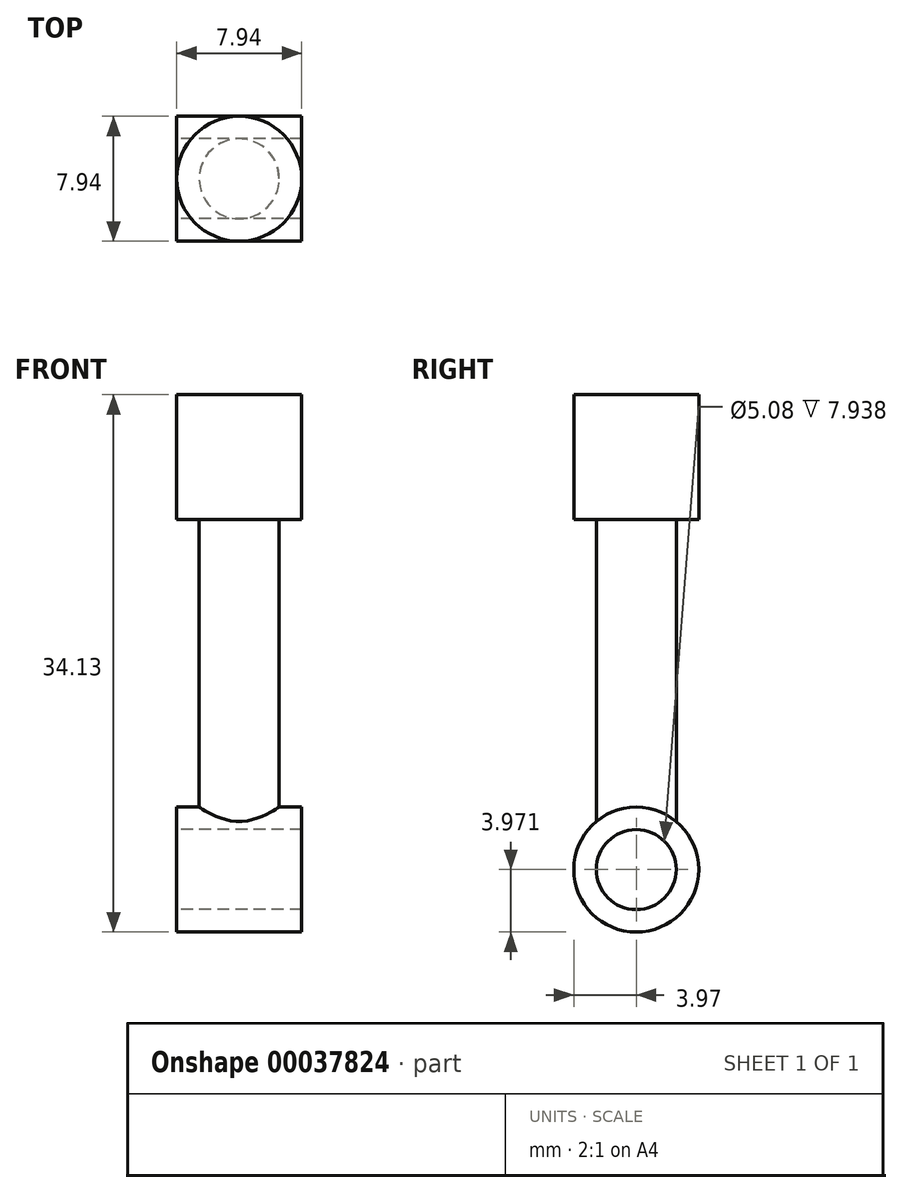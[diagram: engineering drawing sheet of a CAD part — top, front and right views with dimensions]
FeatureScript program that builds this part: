
annotation { "Feature Type Name" : "Feature", "Feature Type Description" : "" }
export const myFeature = defineFeature(function(context is Context, id is Id, definition is map)
    precondition{}
    {
        {
            var Q0;
            Q0=qCreatedBy(makeId("Top.planeOp"),FACE);
            var sketch = newSketch(context, id + "F0", { "sketchPlane" : qUnion([Q0])});
            skCircle(sketch, "E0", {"center": v(0, 0) * mm, "radius": 2.54 * mm});
            skSolve(sketch);
        }
        {
            var Q0;
            Q0 = qSketchRegion(id + "F0", true);
            extrude(context, id + "F1", {"entities" : qUnion([Q0]), "depth" : 18.26 * mm});
        }
        {
            var Q0;
            Q0=makeQuery(id+"F1.opExtrude","CAP_FACE",FACE,{"disambiguationData":[OSD([sQuery(id+"F0.wireOp",EDGE,"E0")])],"isStart":true});
            var sketch = newSketch(context, id + "F2", { "sketchPlane" : qUnion([Q0])});
            skLineSegment(sketch, "E1.rect.bottom", {"start": v(3.97, -3.97) * mm, "end": v(-3.97, -3.97) * mm});
            skLineSegment(sketch, "E1.rect.top", {"start": v(3.97, 3.97) * mm, "end": v(-3.97, 3.97) * mm});
            skLineSegment(sketch, "E1.rect.left", {"start": v(3.97, -3.97) * mm, "end": v(3.97, 3.97) * mm});
            skLineSegment(sketch, "E1.rect.right", {"start": v(-3.97, -3.97) * mm, "end": v(-3.97, 3.97) * mm});
            skPoint(sketch, "E1.rect.middle", {"position": v(0, 0) * mm});
            skSolve(sketch);
        }
        {
            var Q0;
            Q0 = qSketchRegion(id + "F2", true);
            extrude(context, id + "F3", {"entities" : qUnion([Q0]), "operationType" : NewBodyOperationType.ADD, "depth" : 7.94 * mm});
        }
        {
            var Q0;
            Q0=makeQuery(id+"F1.opExtrude","CAP_FACE",FACE,{"disambiguationData":[OSD([sQuery(id+"F0.wireOp",EDGE,"E0")])],"isStart":false});
            var sketch = newSketch(context, id + "F4", { "sketchPlane" : qUnion([Q0])});
            skCircle(sketch, "E2", {"center": v(0, 0) * mm, "radius": 3.97 * mm});
            skSolve(sketch);
        }
        {
            var Q0;
            Q0 = qSketchRegion(id + "F4", true);
            extrude(context, id + "F5", {"entities" : qUnion([Q0]), "operationType" : NewBodyOperationType.ADD, "depth" : 7.94 * mm});
        }
        {
            var Q0;
            Q0=makeQuery(id+"F3.opExtrude","CAP_EDGE",EDGE,{"disambiguationData":[OSD([sQuery(id+"F2.wireOp",EDGE,"E1.rect.top")])],"isStart":true});
            var Q1;
            Q1=makeQuery(id+"F3.opExtrude","CAP_EDGE",EDGE,{"disambiguationData":[OSD([sQuery(id+"F2.wireOp",EDGE,"E1.rect.bottom")])],"isStart":true});
            var Q2;
            Q2=makeQuery(id+"F3.opExtrude","CAP_EDGE",EDGE,{"disambiguationData":[OSD([sQuery(id+"F2.wireOp",EDGE,"E1.rect.bottom")])],"isStart":false});
            var Q3;
            Q3=makeQuery(id+"F3.opExtrude","CAP_EDGE",EDGE,{"disambiguationData":[OSD([sQuery(id+"F2.wireOp",EDGE,"E1.rect.top")])],"isStart":false});
            fillet(context, id + "F6", {"entities" : qUnion([Q0, Q1, Q2, Q3]), "radius" : 3.97 * mm, "tangentPropagation" : true, "allowEdgeOverflow" : false});
        }
        {
            var Q0;
            Q0=makeQuery(id+"F3.opExtrude","SWEPT_FACE",FACE,{"disambiguationData":[OSD([sQuery(id+"F2.wireOp",EDGE,"E1.rect.right")])]});
            var sketch = newSketch(context, id + "F7", { "sketchPlane" : qUnion([Q0])});
            skCircle(sketch, "E3", {"center": v(0, -3.97) * mm, "radius": 2.54 * mm});
            skSolve(sketch);
        }
        {
            var Q0;
            Q0 = qSketchRegion(id + "F7", true);
            var Q1;
            Q1=makeQuery(id+"F3.opExtrude","SWEPT_FACE",FACE,{"disambiguationData":[OSD([sQuery(id+"F2.wireOp",EDGE,"E1.rect.left")])]});
            extrude(context, id + "F8", {"entities" : qUnion([Q0]), "operationType" : NewBodyOperationType.REMOVE, "endBound" : BoundingType.UP_TO_SURFACE, "oppositeDirection" : true, "endBoundEntityFace" : qUnion([Q1]), "depth" : 25.4 * mm});
        }
    });
